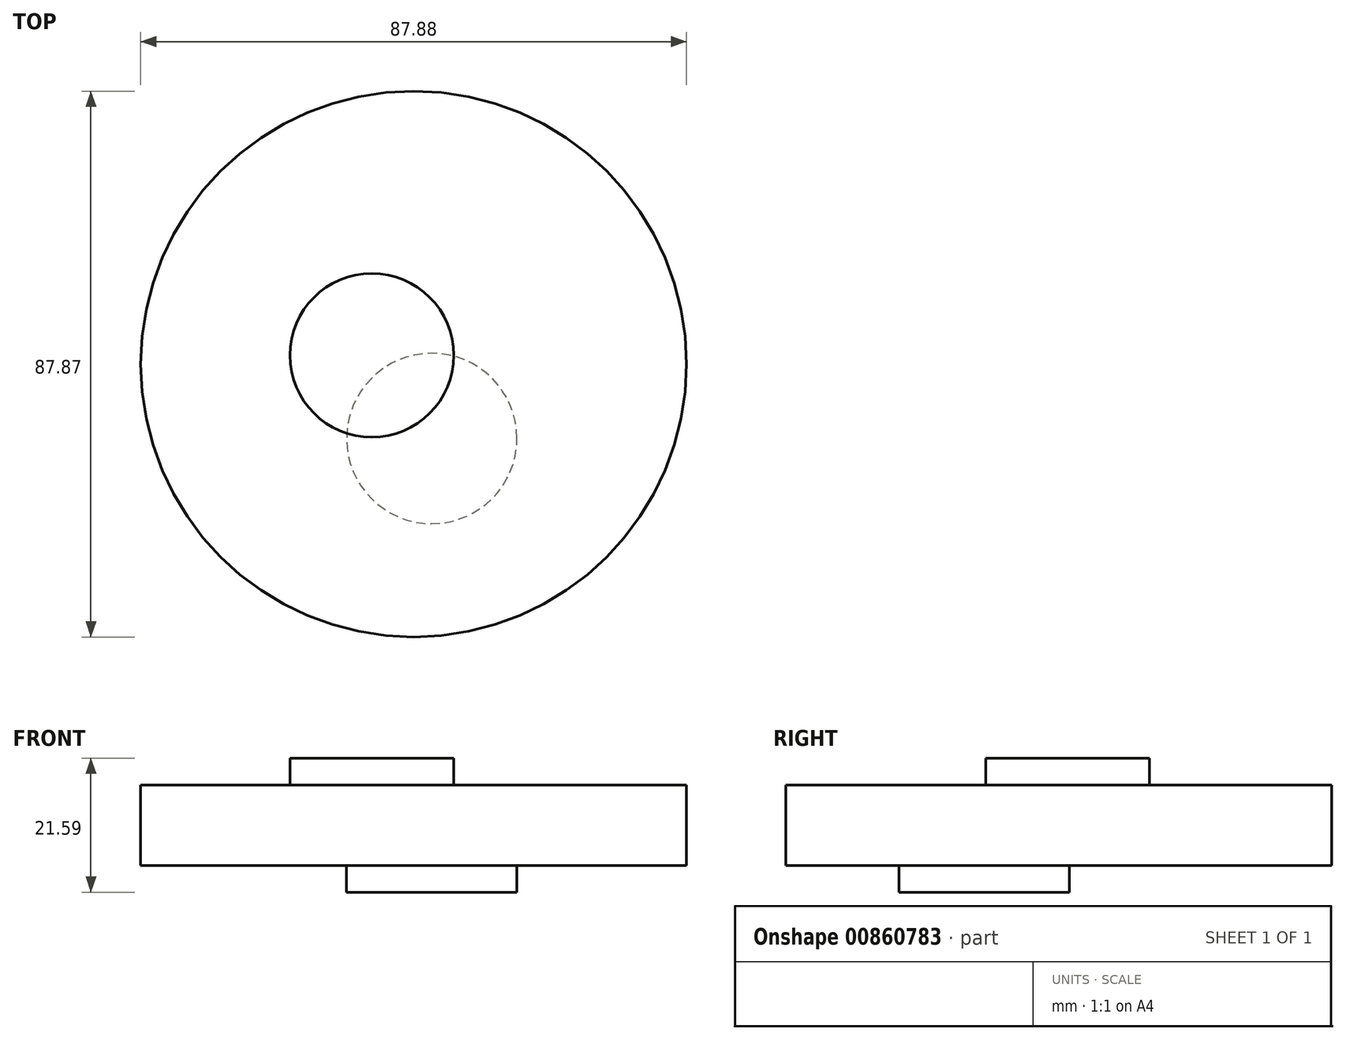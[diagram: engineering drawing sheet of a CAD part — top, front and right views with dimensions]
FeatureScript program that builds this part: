
annotation { "Feature Type Name" : "Feature", "Feature Type Description" : "" }
export const myFeature = defineFeature(function(context is Context, id is Id, definition is map)
    precondition{}
    {
        {
            var Q0;
            Q0=qCreatedBy(makeId("Top.planeOp"),FACE);
            var sketch = newSketch(context, id + "F0", { "sketchPlane" : qUnion([Q0])});
            skCircle(sketch, "E0", {"center": v(-21.18, 11.98) * mm, "radius": 43.94 * mm});
            skSolve(sketch);
        }
        {
            var Q0;
            Q0=makeQuery(id+"F0.imprint","IMPRINT",FACE,{"disambiguationData":[TD([[makeQuery(id+"F0.imprint","IMPRINT",EDGE,{"derivedFrom":sQuery(id+"F0.wireOp",EDGE,"E0")}),1.0]])]});
            extrude(context, id + "F1", {"entities" : qUnion([Q0]), "depth" : 12.95 * mm, "offsetDistance" : 25.4 * mm});
        }
        {
            var Q0;
            Q0=makeQuery(id+"F1.opExtrude","CAP_FACE",FACE,{"disambiguationData":[OSD([sQuery(id+"F0.wireOp",EDGE,"E0")])],"isStart":false});
            var sketch = newSketch(context, id + "F2", { "sketchPlane" : qUnion([Q0])});
            skCircle(sketch, "E1", {"center": v(-27.9, 13.4) * mm, "radius": 13.19 * mm});
            skSolve(sketch);
        }
        {
            var Q0;
            Q0=makeQuery(id+"F2.imprint","IMPRINT",FACE,{"disambiguationData":[TD([[makeQuery(id+"F2.imprint","IMPRINT",EDGE,{"derivedFrom":sQuery(id+"F2.wireOp",EDGE,"E1")}),1.0]])]});
            extrude(context, id + "F3", {"entities" : qUnion([Q0]), "operationType" : NewBodyOperationType.ADD, "depth" : 4.32 * mm, "offsetDistance" : 25.4 * mm});
        }
        {
            var Q0;
            Q0=makeQuery(id+"F1.opExtrude","CAP_FACE",FACE,{"disambiguationData":[OSD([sQuery(id+"F0.wireOp",EDGE,"E0")])],"isStart":true});
            var sketch = newSketch(context, id + "F4", { "sketchPlane" : qUnion([Q0])});
            skCircle(sketch, "E2", {"center": v(-18.26, 0) * mm, "radius": 13.72 * mm});
            skSolve(sketch);
        }
        {
            var Q0;
            Q0=makeQuery(id+"F4.imprint","IMPRINT",FACE,{"disambiguationData":[TD([[makeQuery(id+"F4.imprint","IMPRINT",EDGE,{"derivedFrom":sQuery(id+"F4.wireOp",EDGE,"E2")}),1.0]])]});
            extrude(context, id + "F5", {"entities" : qUnion([Q0]), "operationType" : NewBodyOperationType.ADD, "depth" : 4.32 * mm, "offsetDistance" : 25.4 * mm});
        }
    });
